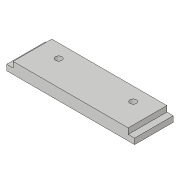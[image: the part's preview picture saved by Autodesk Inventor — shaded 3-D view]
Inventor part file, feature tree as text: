
AUTODESK INVENTOR PART (.ipt)
format: ipt  version: 2018.3 (Build 223284000, 284)  size: 108,032 bytes
history: native  units: in
note: dims shown in document units (in); Inventor stores cm internally (conversion verified against a paired STEP export)
features: extrude x3, sketch x3
ambient origin geometry x8: Origin, YZ Plane, XZ Plane, XY Plane, X Axis, Y Axis, Z Axis, Center Point
bodies: Solid1 (feature_tree)
feature tree (6):
  extrude  "Extrusion1"  Depth=0.756in
  extrude  "Extrusion6"  Depth=0.221in
  extrude  "Extrusion7"  Depth=0.1105in
  sketch  "Sketch1"  dims[d0=2.5in d1=0.756in]
  sketch  "Sketch7"  dims[d2=0.221in d3=0.0in d22=0.126in]
  sketch  "Sketch8"  dims[d23=0.126in d24=1.4567in d32=1.0in d33=0.0in d34=0.125in d35=0.125in d36=0.1105in d37=0.0in d38=0.4941in d39=0.5217in d40=0.5217in]
